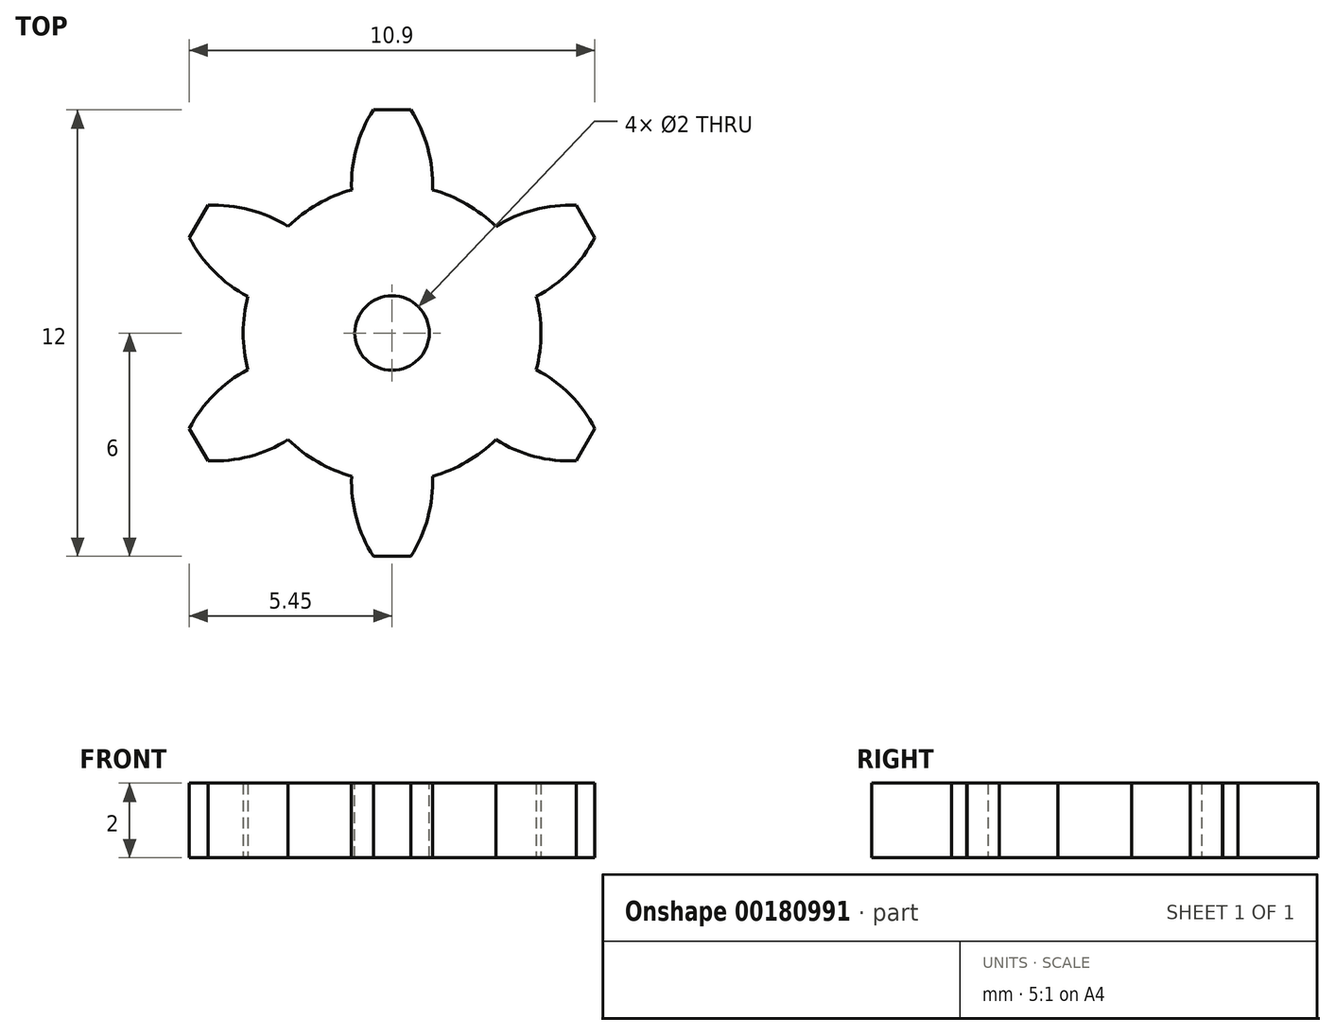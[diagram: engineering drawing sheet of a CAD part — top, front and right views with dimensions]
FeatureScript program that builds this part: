
annotation { "Feature Type Name" : "Feature", "Feature Type Description" : "" }
export const myFeature = defineFeature(function(context is Context, id is Id, definition is map)
    precondition{}
    {
        {
            var Q0;
            Q0=qCreatedBy(makeId("Top.planeOp"),FACE);
            var sketch = newSketch(context, id + "F0", { "sketchPlane" : qUnion([Q0])});
            skCircle(sketch, "E0", {"center": v(0, 0) * mm, "radius": 4 * mm});
            skLineSegment(sketch, "E1", {"start": v(0, 0) * mm, "end": v(0, 4) * mm, "construction": true});
            skLineSegment(sketch, "E2", {"start": v(0, 4) * mm, "end": v(0, 6) * mm});
            skLineSegment(sketch, "E3", {"start": v(0, 6) * mm, "end": v(-0.5, 6) * mm});
            skArc(sketch, "E4", {"start": v(-0.5, 6) * mm, "mid": v(-0.96, 4.97) * mm, "end": v(-1.09, 3.85) * mm});
            skLineSegment(sketch, "E5.MirrorCS", {"start": v(0, 6) * mm, "end": v(0.5, 6) * mm});
            skArc(sketch, "E6.MirrorCS", {"start": v(0.5, 6) * mm, "mid": v(0.96, 4.97) * mm, "end": v(1.09, 3.85) * mm});
            skArc(sketch, "E7.1.0", {"start": v(-5.45, 2.57) * mm, "mid": v(-4.78, 1.65) * mm, "end": v(-3.88, 0.98) * mm});
            skLineSegment(sketch, "E7.1.1", {"start": v(-5.2, 3) * mm, "end": v(-5.45, 2.57) * mm});
            skLineSegment(sketch, "E7.1.2", {"start": v(-5.2, 3) * mm, "end": v(-4.95, 3.43) * mm});
            skArc(sketch, "E7.1.3", {"start": v(-4.95, 3.43) * mm, "mid": v(-3.82, 3.32) * mm, "end": v(-2.8, 2.87) * mm});
            skArc(sketch, "E7.2.0", {"start": v(-4.95, -3.43) * mm, "mid": v(-3.82, -3.32) * mm, "end": v(-2.8, -2.87) * mm});
            skLineSegment(sketch, "E7.2.1", {"start": v(-5.2, -3) * mm, "end": v(-4.95, -3.43) * mm});
            skLineSegment(sketch, "E7.2.2", {"start": v(-5.2, -3) * mm, "end": v(-5.45, -2.57) * mm});
            skArc(sketch, "E7.2.3", {"start": v(-5.45, -2.57) * mm, "mid": v(-4.78, -1.65) * mm, "end": v(-3.88, -0.98) * mm});
            skArc(sketch, "E7.3.0", {"start": v(0.5, -6) * mm, "mid": v(0.96, -4.97) * mm, "end": v(1.09, -3.85) * mm});
            skLineSegment(sketch, "E7.3.1", {"start": v(0, -6) * mm, "end": v(0.5, -6) * mm});
            skLineSegment(sketch, "E7.3.2", {"start": v(0, -6) * mm, "end": v(-0.5, -6) * mm});
            skArc(sketch, "E7.3.3", {"start": v(-0.5, -6) * mm, "mid": v(-0.96, -4.97) * mm, "end": v(-1.09, -3.85) * mm});
            skArc(sketch, "E7.4.0", {"start": v(5.45, -2.57) * mm, "mid": v(4.78, -1.65) * mm, "end": v(3.88, -0.98) * mm});
            skLineSegment(sketch, "E7.4.1", {"start": v(5.2, -3) * mm, "end": v(5.45, -2.57) * mm});
            skLineSegment(sketch, "E7.4.2", {"start": v(5.2, -3) * mm, "end": v(4.95, -3.43) * mm});
            skArc(sketch, "E7.4.3", {"start": v(4.95, -3.43) * mm, "mid": v(3.82, -3.32) * mm, "end": v(2.8, -2.87) * mm});
            skArc(sketch, "E7.5.0", {"start": v(4.95, 3.43) * mm, "mid": v(3.82, 3.32) * mm, "end": v(2.8, 2.87) * mm});
            skLineSegment(sketch, "E7.5.1", {"start": v(5.2, 3) * mm, "end": v(4.95, 3.43) * mm});
            skLineSegment(sketch, "E7.5.2", {"start": v(5.2, 3) * mm, "end": v(5.45, 2.57) * mm});
            skArc(sketch, "E7.5.3", {"start": v(5.45, 2.57) * mm, "mid": v(4.78, 1.65) * mm, "end": v(3.88, 0.98) * mm});
            skSolve(sketch);
        }
        {
            var Q0;
            Q0 = qSketchRegion(id + "F0", true);
            extrude(context, id + "F1", {"entities" : qUnion([Q0]), "depth" : 2 * mm});
        }
        {
            var Q0;
            Q0=makeQuery(id+"F1.opExtrude","CAP_FACE",FACE,{"disambiguationData":[OSD([sQuery(id+"F0.wireOp",EDGE,"E0"),sQuery(id+"F0.wireOp",EDGE,"E3"),sQuery(id+"F0.wireOp",EDGE,"E4"),sQuery(id+"F0.wireOp",EDGE,"E5.MirrorCS"),sQuery(id+"F0.wireOp",EDGE,"E6.MirrorCS"),sQuery(id+"F0.wireOp",EDGE,"E7.1.0"),sQuery(id+"F0.wireOp",EDGE,"E7.1.1"),sQuery(id+"F0.wireOp",EDGE,"E7.1.2"),sQuery(id+"F0.wireOp",EDGE,"E7.1.3"),sQuery(id+"F0.wireOp",EDGE,"E7.2.0"),sQuery(id+"F0.wireOp",EDGE,"E7.2.1"),sQuery(id+"F0.wireOp",EDGE,"E7.2.2"),sQuery(id+"F0.wireOp",EDGE,"E7.2.3"),sQuery(id+"F0.wireOp",EDGE,"E7.3.0"),sQuery(id+"F0.wireOp",EDGE,"E7.3.1"),sQuery(id+"F0.wireOp",EDGE,"E7.3.2"),sQuery(id+"F0.wireOp",EDGE,"E7.3.3"),sQuery(id+"F0.wireOp",EDGE,"E7.4.0"),sQuery(id+"F0.wireOp",EDGE,"E7.4.1"),sQuery(id+"F0.wireOp",EDGE,"E7.4.2"),sQuery(id+"F0.wireOp",EDGE,"E7.4.3"),sQuery(id+"F0.wireOp",EDGE,"E7.5.0"),sQuery(id+"F0.wireOp",EDGE,"E7.5.1"),sQuery(id+"F0.wireOp",EDGE,"E7.5.2"),sQuery(id+"F0.wireOp",EDGE,"E7.5.3"),sQuery(id+"F0.wireOp",EDGE,"E7.6.0"),sQuery(id+"F0.wireOp",EDGE,"E7.6.1"),sQuery(id+"F0.wireOp",EDGE,"E7.6.2"),sQuery(id+"F0.wireOp",EDGE,"E7.6.3"),sQuery(id+"F0.wireOp",EDGE,"E7.7.0"),sQuery(id+"F0.wireOp",EDGE,"E7.7.1"),sQuery(id+"F0.wireOp",EDGE,"E7.7.2"),sQuery(id+"F0.wireOp",EDGE,"E7.7.3")])],"isStart":false});
            var sketch = newSketch(context, id + "F2", { "sketchPlane" : qUnion([Q0])});
            skCircle(sketch, "E8", {"center": v(0, 0) * mm, "radius": 1 * mm});
            skSolve(sketch);
        }
        {
            var Q0;
            Q0 = qSketchRegion(id + "F2", true);
            extrude(context, id + "F3", {"entities" : qUnion([Q0]), "operationType" : NewBodyOperationType.REMOVE, "endBound" : BoundingType.THROUGH_ALL, "oppositeDirection" : true, "depth" : 25 * mm});
        }
    });
